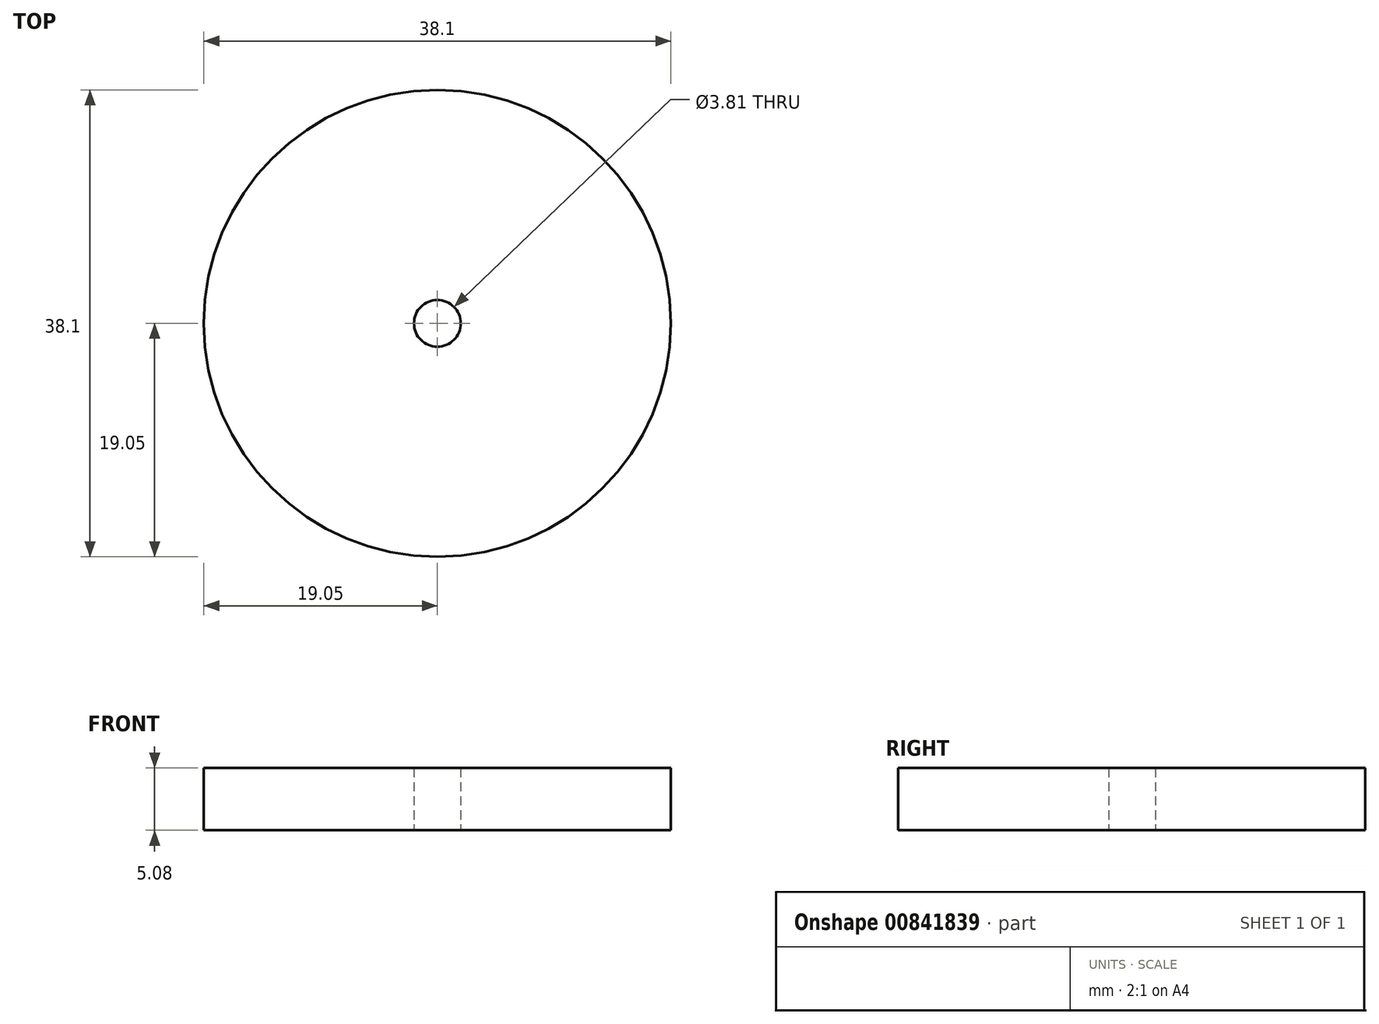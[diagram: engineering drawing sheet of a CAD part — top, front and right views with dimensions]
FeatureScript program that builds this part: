
annotation { "Feature Type Name" : "Feature", "Feature Type Description" : "" }
export const myFeature = defineFeature(function(context is Context, id is Id, definition is map)
    precondition{}
    {
        {
            var Q0;
            Q0=qCreatedBy(makeId("Top.planeOp"),FACE);
            var sketch = newSketch(context, id + "F0", { "sketchPlane" : qUnion([Q0])});
            skCircle(sketch, "E0", {"center": v(0, 0) * mm, "radius": 19.05 * mm});
            skCircle(sketch, "E1", {"center": v(0, 0) * mm, "radius": 1.9 * mm});
            skSolve(sketch);
        }
        {
            var Q0;
            Q0=makeQuery(id+"F0.imprint","IMPRINT",FACE,{"disambiguationData":[TD([[makeQuery(id+"F0.imprint","IMPRINT",EDGE,{"derivedFrom":sQuery(id+"F0.wireOp",EDGE,"E0")}),1.0]])]});
            extrude(context, id + "F1", {"entities" : qUnion([Q0]), "depth" : 5.08 * mm, "offsetDistance" : 25.4 * mm});
        }
    });
